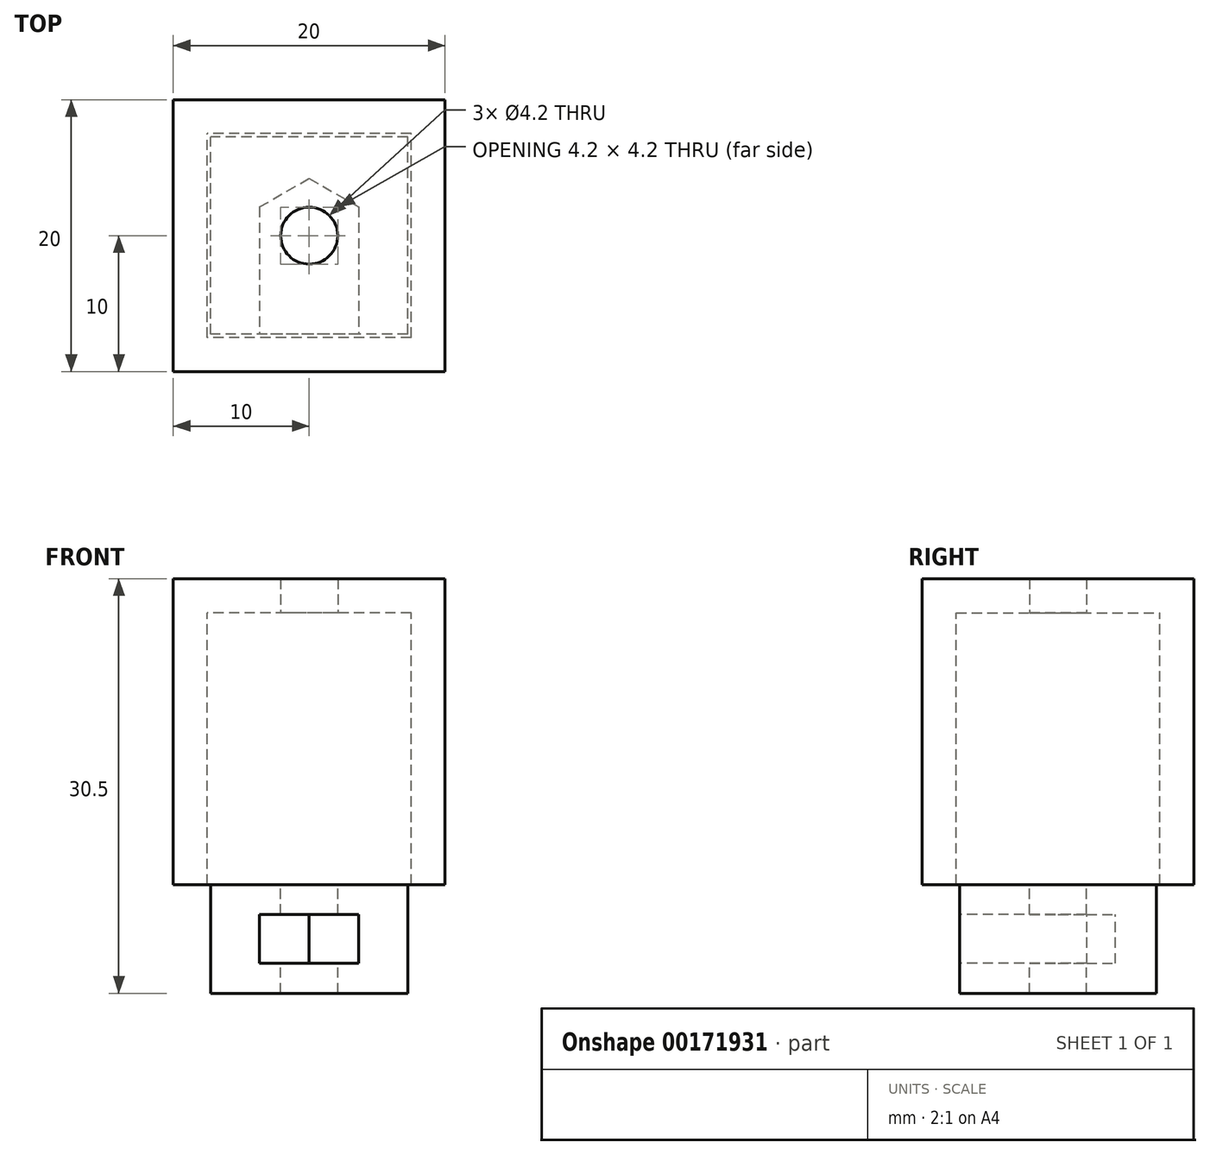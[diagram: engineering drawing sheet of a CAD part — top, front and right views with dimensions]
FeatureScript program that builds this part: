
annotation { "Feature Type Name" : "Feature", "Feature Type Description" : "" }
export const myFeature = defineFeature(function(context is Context, id is Id, definition is map)
    precondition{}
    {
        {
            var Q0;
            Q0=qCreatedBy(makeId("Top.planeOp"),FACE);
            var sketch = newSketch(context, id + "F0", { "sketchPlane" : qUnion([Q0])});
            skLineSegment(sketch, "E0.bottom", {"start": v(10, -10) * mm, "end": v(-10, -10) * mm});
            skLineSegment(sketch, "E0.top", {"start": v(10, 10) * mm, "end": v(-10, 10) * mm});
            skLineSegment(sketch, "E0.left", {"start": v(10, -10) * mm, "end": v(10, 10) * mm});
            skLineSegment(sketch, "E0.right", {"start": v(-10, -10) * mm, "end": v(-10, 10) * mm});
            skPoint(sketch, "E0.middle", {"position": v(0, 0) * mm});
            skCircle(sketch, "E1", {"center": v(0, 0) * mm, "radius": 2.1 * mm});
            skLineSegment(sketch, "E2.0", {"start": v(-7.5, -7.5) * mm, "end": v(-7.5, 7.5) * mm});
            skLineSegment(sketch, "E2.1", {"start": v(7.5, -7.5) * mm, "end": v(-7.5, -7.5) * mm});
            skLineSegment(sketch, "E2.2", {"start": v(7.5, -7.5) * mm, "end": v(7.5, 7.5) * mm});
            skLineSegment(sketch, "E2.3", {"start": v(7.5, 7.5) * mm, "end": v(-7.5, 7.5) * mm});
            skSolve(sketch);
        }
        {
            var Q0;
            Q0 = qSketchRegion(id + "F0", true);
            var Q1;
            Q1=makeQuery(id+"F0.imprint","IMPRINT",FACE,{"disambiguationData":[TD([[makeQuery(id+"F0.imprint","IMPRINT",EDGE,{"derivedFrom":sQuery(id+"F0.wireOp",EDGE,"E1")}),-1.0]])]});
            extrude(context, id + "F1", {"entities" : qUnion([Q0, Q1]), "depth" : 2.5 * mm});
        }
        {
            var Q0;
            Q0=makeQuery(id+"F0.imprint","IMPRINT",FACE,{"disambiguationData":[TD([[makeQuery(id+"F0.imprint","IMPRINT",EDGE,{"derivedFrom":sQuery(id+"F0.wireOp",EDGE,"E0.bottom")}),-1.0]])]});
            extrude(context, id + "F2", {"entities" : qUnion([Q0]), "operationType" : NewBodyOperationType.ADD, "oppositeDirection" : true, "depth" : 20 * mm});
        }
        {
            var Q0;
            Q0=makeQuery(id+"F2.opExtrude","CAP_FACE",FACE,{"disambiguationData":[OSD([sQuery(id+"F0.wireOp",EDGE,"E0.bottom"),sQuery(id+"F0.wireOp",EDGE,"E0.top"),sQuery(id+"F0.wireOp",EDGE,"E0.left"),sQuery(id+"F0.wireOp",EDGE,"E0.right"),sQuery(id+"F0.wireOp",EDGE,"E2.0"),sQuery(id+"F0.wireOp",EDGE,"E2.1"),sQuery(id+"F0.wireOp",EDGE,"E2.2"),sQuery(id+"F0.wireOp",EDGE,"E2.3")])],"isStart":false});
            var sketch = newSketch(context, id + "F3", { "sketchPlane" : qUnion([Q0])});
            skCircle(sketch, "E3.cCircle", {"center": v(0, 0) * mm, "radius": 3.65 * mm, "construction": true});
            skPoint(sketch, "E3.cCircle.perimeterSnap0", {"position": v(-7.5, 0) * mm});
            skLineSegment(sketch, "E3.0", {"start": v(-3.65, -2.1) * mm, "end": v(-3.65, 2.1) * mm});
            skLineSegment(sketch, "E3.1", {"start": v(-3.65, 2.1) * mm, "end": v(0, 4.21) * mm});
            skLineSegment(sketch, "E3.2", {"start": v(0, 4.21) * mm, "end": v(3.65, 2.1) * mm});
            skLineSegment(sketch, "E3.3", {"start": v(3.65, 2.1) * mm, "end": v(3.65, -2.1) * mm});
            skLineSegment(sketch, "E3.4", {"start": v(3.65, -2.1) * mm, "end": v(0, -4.21) * mm});
            skLineSegment(sketch, "E3.5", {"start": v(0, -4.21) * mm, "end": v(-3.65, -2.1) * mm});
            skPoint(sketch, "E3.0.midPoint", {"position": v(-3.65, 0) * mm});
            skPoint(sketch, "E3.0.midPoint.positionSnap0", {"position": v(-7.5, 0) * mm});
            skLineSegment(sketch, "E4.bottom", {"start": v(7.25, 7.25) * mm, "end": v(-7.25, 7.25) * mm});
            skLineSegment(sketch, "E4.top", {"start": v(7.25, -7.25) * mm, "end": v(-7.25, -7.25) * mm});
            skLineSegment(sketch, "E4.left", {"start": v(7.25, 7.25) * mm, "end": v(7.25, -7.25) * mm});
            skLineSegment(sketch, "E4.right", {"start": v(-7.25, 7.25) * mm, "end": v(-7.25, -7.25) * mm});
            skSolve(sketch);
        }
        {
            var Q0;
            Q0 = qSketchRegion(id + "F3", true);
            extrude(context, id + "F4", {"entities" : qUnion([Q0]), "depth" : 4 * mm});
        }
        {
            var Q0;
            Q0=makeQuery(id+"F4.opExtrude","CAP_FACE",FACE,{"disambiguationData":[OSD([sQuery(id+"F3.wireOp",EDGE,"E3.0"),sQuery(id+"F3.wireOp",EDGE,"E3.1"),sQuery(id+"F3.wireOp",EDGE,"E3.2"),sQuery(id+"F3.wireOp",EDGE,"E3.3"),sQuery(id+"F3.wireOp",EDGE,"E3.4"),sQuery(id+"F3.wireOp",EDGE,"E3.5"),sQuery(id+"F3.wireOp",EDGE,"E4.bottom"),sQuery(id+"F3.wireOp",EDGE,"E4.top"),sQuery(id+"F3.wireOp",EDGE,"E4.left"),sQuery(id+"F3.wireOp",EDGE,"E4.right")])],"isStart":false});
            var sketch = newSketch(context, id + "F5", { "sketchPlane" : qUnion([Q0])});
            skLineSegment(sketch, "E5", {"start": v(-3.65, -2.1) * mm, "end": v(-3.65, -7.25) * mm});
            skLineSegment(sketch, "E6", {"start": v(3.65, -2.1) * mm, "end": v(3.65, -7.25) * mm});
            skLineSegment(sketch, "E7", {"start": v(-3.65, -7.25) * mm, "end": v(3.65, -7.25) * mm});
            skSolve(sketch);
        }
        {
            var Q0;
            Q0 = qSketchRegion(id + "F5", true);
            var Q1;
            Q1=makeQuery(id+"F5.imprint","IMPRINT",FACE,{"disambiguationData":[TD([[makeQuery(id+"F5.imprint","IMPRINT",EDGE,{"derivedFrom":sQuery(id+"F5.wireOp",EDGE,"E5")}),1.0]])]});
            extrude(context, id + "F6", {"entities" : qUnion([Q0, Q1]), "operationType" : NewBodyOperationType.REMOVE, "oppositeDirection" : true, "depth" : 1.7 * mm});
        }
        {
            var Q0;
            Q0=makeQuery(id+"F4.opExtrude","CAP_FACE",FACE,{"disambiguationData":[OSD([sQuery(id+"F3.wireOp",EDGE,"E3.0"),sQuery(id+"F3.wireOp",EDGE,"E3.1"),sQuery(id+"F3.wireOp",EDGE,"E3.2"),sQuery(id+"F3.wireOp",EDGE,"E3.3"),sQuery(id+"F3.wireOp",EDGE,"E3.4"),sQuery(id+"F3.wireOp",EDGE,"E3.5"),sQuery(id+"F3.wireOp",EDGE,"E4.bottom"),sQuery(id+"F3.wireOp",EDGE,"E4.top"),sQuery(id+"F3.wireOp",EDGE,"E4.left"),sQuery(id+"F3.wireOp",EDGE,"E4.right")])],"isStart":false});
            extrude(context, id + "F7", {"entities" : qUnion([Q0]), "operationType" : NewBodyOperationType.ADD, "depth" : 4 * mm});
        }
        {
            var Q0;
            Q0=makeQuery(id+"F6.boolean.opBoolean","COPY",FACE,{"derivedFrom":makeQuery(id+"F6.opExtrude","CAP_FACE",FACE,{"disambiguationData":[OSD([sQuery(id+"F3.wireOp",EDGE,"E3.4"),sQuery(id+"F3.wireOp",EDGE,"E3.5"),sQuery(id+"F5.wireOp",EDGE,"E5"),sQuery(id+"F5.wireOp",EDGE,"E6"),sQuery(id+"F5.wireOp",EDGE,"E7")])],"isStart":false})});
            var Q1;
            Q1=makeQuery(id+"F7.opExtrude","CAP_FACE",FACE,{"disambiguationData":[OSD([sQuery(id+"F3.wireOp",EDGE,"E3.0"),sQuery(id+"F3.wireOp",EDGE,"E3.1"),sQuery(id+"F3.wireOp",EDGE,"E3.2"),sQuery(id+"F3.wireOp",EDGE,"E3.3"),sQuery(id+"F3.wireOp",EDGE,"E3.4"),sQuery(id+"F3.wireOp",EDGE,"E3.5"),sQuery(id+"F3.wireOp",EDGE,"E4.bottom"),sQuery(id+"F3.wireOp",EDGE,"E4.top"),sQuery(id+"F3.wireOp",EDGE,"E4.left"),sQuery(id+"F3.wireOp",EDGE,"E4.right")])],"isStart":false});
            extrude(context, id + "F8", {"entities" : qUnion([Q0]), "operationType" : NewBodyOperationType.ADD, "endBound" : BoundingType.UP_TO_SURFACE, "endBoundEntityFace" : qUnion([Q1]), "depth" : 25 * mm});
        }
        {
            var Q0;
            {var subQ0=sQuery(id+"F3.wireOp",EDGE,"E4.bottom");Q0=makeQuery(id+"F7.boolean.opBoolean","MERGE",FACE,{"derivedFrom":[makeQuery(id+"F4.opExtrude","SWEPT_FACE",FACE,{"disambiguationData":[OSD([subQ0])]}),makeQuery(id+"F7.opExtrude","SWEPT_FACE",FACE,{"disambiguationData":[OSD([subQ0])]})]});}
            var sketch = newSketch(context, id + "F9", { "sketchPlane" : qUnion([Q0])});
            skLineSegment(sketch, "E8.bottom", {"start": v(3.65, -25.8) * mm, "end": v(-3.65, -25.8) * mm});
            skLineSegment(sketch, "E8.top", {"start": v(3.65, -22.2) * mm, "end": v(-3.65, -22.2) * mm});
            skLineSegment(sketch, "E8.left", {"start": v(3.65, -25.8) * mm, "end": v(3.65, -22.2) * mm});
            skLineSegment(sketch, "E8.right", {"start": v(-3.65, -25.8) * mm, "end": v(-3.65, -22.2) * mm});
            skSolve(sketch);
        }
        {
            var Q0;
            Q0 = qSketchRegion(id + "F9", true);
            extrude(context, id + "F10", {"entities" : qUnion([Q0]), "operationType" : NewBodyOperationType.REMOVE, "oppositeDirection" : true, "depth" : 7.2 * mm});
        }
        {
            var Q0;
            {var subQ0=sQuery(id+"F3.wireOp",EDGE,"E3.5");var subQ1=sQuery(id+"F3.wireOp",EDGE,"E3.4");Q0=makeQuery(id+"F8.boolean.opBoolean","MERGE",FACE,{"derivedFrom":[makeQuery(id+"F7.opExtrude","CAP_FACE",FACE,{"disambiguationData":[OSD([sQuery(id+"F3.wireOp",EDGE,"E3.0"),sQuery(id+"F3.wireOp",EDGE,"E3.1"),sQuery(id+"F3.wireOp",EDGE,"E3.2"),sQuery(id+"F3.wireOp",EDGE,"E3.3"),subQ1,subQ0,sQuery(id+"F3.wireOp",EDGE,"E4.bottom"),sQuery(id+"F3.wireOp",EDGE,"E4.top"),sQuery(id+"F3.wireOp",EDGE,"E4.left"),sQuery(id+"F3.wireOp",EDGE,"E4.right")])],"isStart":false}),makeQuery(id+"F8.opExtrude","CAP_FACE",FACE,{"disambiguationData":[OSD([subQ1,subQ0,sQuery(id+"F5.wireOp",EDGE,"E5"),sQuery(id+"F5.wireOp",EDGE,"E6"),sQuery(id+"F5.wireOp",EDGE,"E7")])],"isStart":false})]});}
            var sketch = newSketch(context, id + "F11", { "sketchPlane" : qUnion([Q0])});
            skLineSegment(sketch, "E9.bottom", {"start": v(-7.25, 7.25) * mm, "end": v(7.25, 7.25) * mm});
            skLineSegment(sketch, "E9.top", {"start": v(-7.25, -7.25) * mm, "end": v(7.25, -7.25) * mm});
            skLineSegment(sketch, "E9.left", {"start": v(-7.25, 7.25) * mm, "end": v(-7.25, -7.25) * mm});
            skLineSegment(sketch, "E9.right", {"start": v(7.25, 7.25) * mm, "end": v(7.25, -7.25) * mm});
            skSolve(sketch);
        }
        {
            var Q0;
            Q0 = qSketchRegion(id + "F11", true);
            var Q1;
            Q1=makeQuery(id+"F10.boolean.opBoolean","COPY",FACE,{"derivedFrom":makeQuery(id+"F10.opExtrude","SWEPT_FACE",FACE,{"disambiguationData":[OSD([sQuery(id+"F9.wireOp",EDGE,"E8.bottom")])]})});
            extrude(context, id + "F12", {"entities" : qUnion([Q0]), "operationType" : NewBodyOperationType.ADD, "endBound" : BoundingType.UP_TO_SURFACE, "oppositeDirection" : true, "endBoundEntityFace" : qUnion([Q1]), "depth" : 25 * mm});
        }
        {
            var Q0;
            Q0=makeQuery(id+"F4.opExtrude","CAP_FACE",FACE,{"disambiguationData":[OSD([sQuery(id+"F3.wireOp",EDGE,"E3.0"),sQuery(id+"F3.wireOp",EDGE,"E3.1"),sQuery(id+"F3.wireOp",EDGE,"E3.2"),sQuery(id+"F3.wireOp",EDGE,"E3.3"),sQuery(id+"F3.wireOp",EDGE,"E3.4"),sQuery(id+"F3.wireOp",EDGE,"E3.5"),sQuery(id+"F3.wireOp",EDGE,"E4.bottom"),sQuery(id+"F3.wireOp",EDGE,"E4.top"),sQuery(id+"F3.wireOp",EDGE,"E4.left"),sQuery(id+"F3.wireOp",EDGE,"E4.right")])],"isStart":true});
            var sketch = newSketch(context, id + "F13", { "sketchPlane" : qUnion([Q0])});
            skLineSegment(sketch, "E10.bottom", {"start": v(-7.25, -7.25) * mm, "end": v(7.25, -7.25) * mm});
            skLineSegment(sketch, "E10.top", {"start": v(-7.25, 7.25) * mm, "end": v(7.25, 7.25) * mm});
            skLineSegment(sketch, "E10.left", {"start": v(-7.25, -7.25) * mm, "end": v(-7.25, 7.25) * mm});
            skLineSegment(sketch, "E10.right", {"start": v(7.25, -7.25) * mm, "end": v(7.25, 7.25) * mm});
            skSolve(sketch);
        }
        {
            var Q0;
            Q0 = qSketchRegion(id + "F13", true);
            var Q1;
            Q1=makeQuery(id+"F10.boolean.opBoolean","COPY",FACE,{"derivedFrom":makeQuery(id+"F10.opExtrude","SWEPT_FACE",FACE,{"disambiguationData":[OSD([sQuery(id+"F9.wireOp",EDGE,"E8.top")])]})});
            extrude(context, id + "F14", {"entities" : qUnion([Q0]), "operationType" : NewBodyOperationType.ADD, "endBound" : BoundingType.UP_TO_SURFACE, "oppositeDirection" : true, "endBoundEntityFace" : qUnion([Q1]), "depth" : 1.9 * mm});
        }
        {
            var Q0;
            Q0=makeQuery(id+"F1.opExtrude","CAP_FACE",FACE,{"disambiguationData":[OSD([sQuery(id+"F0.wireOp",EDGE,"E0.bottom"),sQuery(id+"F0.wireOp",EDGE,"E0.top"),sQuery(id+"F0.wireOp",EDGE,"E0.left"),sQuery(id+"F0.wireOp",EDGE,"E0.right"),sQuery(id+"F0.wireOp",EDGE,"E1")])],"isStart":false});
            var sketch = newSketch(context, id + "F15", { "sketchPlane" : qUnion([Q0])});
            skCircle(sketch, "E11", {"center": v(0, 0) * mm, "radius": 2.1 * mm});
            skSolve(sketch);
        }
        {
            var Q0;
            Q0 = qSketchRegion(id + "F15", true);
            extrude(context, id + "F16", {"entities" : qUnion([Q0]), "operationType" : NewBodyOperationType.REMOVE, "oppositeDirection" : true, "depth" : 53.6 * mm});
        }
    });
